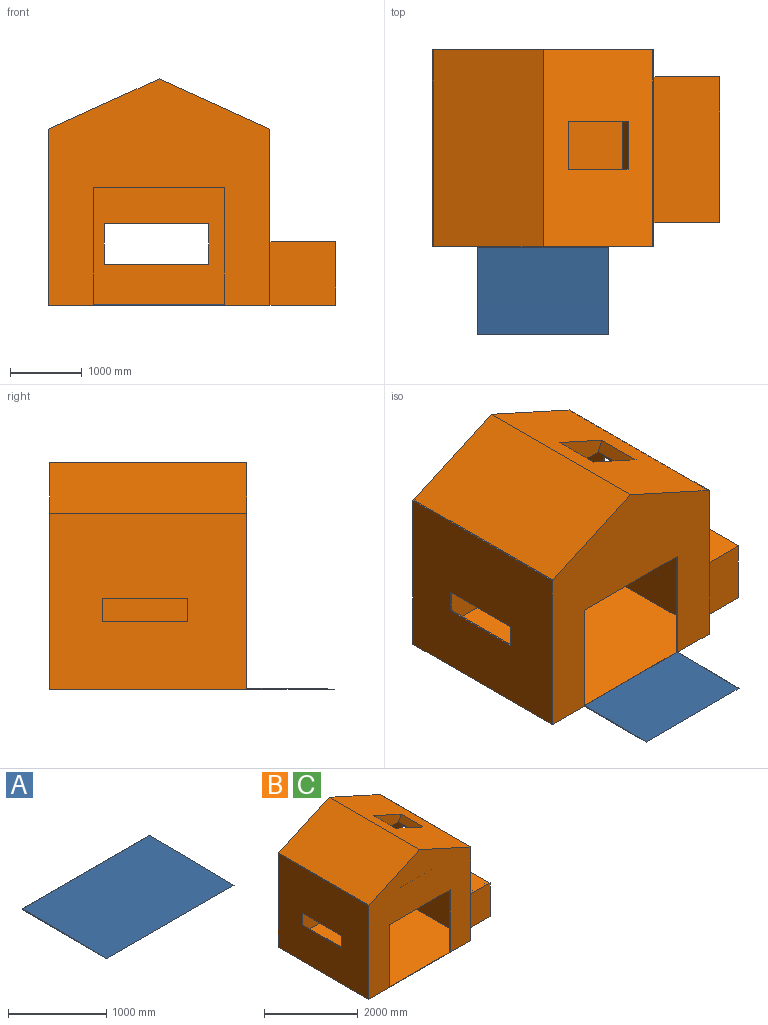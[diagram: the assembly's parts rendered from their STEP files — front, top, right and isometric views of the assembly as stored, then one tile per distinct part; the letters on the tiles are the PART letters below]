
ASSEMBLY  parts=3 mates=1
PART A: 6 faces, bbox 1828.8x1219.2x12.7 mm
  f0: plane 1219.2x12.7mm, normal (-1,0,0), area 10334.8mm2, adj f1,f3,f4,f5
  f1: plane 1828.8x1219.2mm, normal (0,0,-1), area 2229673mm2, adj f0,f2,f4,f5
  f2: plane 1219.2x12.7mm, normal (1,0,0), area 10334.8mm2, adj f1,f3,f4,f5
  f3: plane 1828.8x2.85mm, normal (0,0,1), area 5206.3mm2, adj f0,f2,f4,f5
  f4: plane 1828.8x12.7mm, normal (0,1,0), area 23225.8mm2, adj f0,f1,f2,f3
  f5: cylinder r=58254.97mm len=1828.8mm, axis (-1,0,0), area 2224628.3mm2, adj f0,f1,f2,f3
PART B: 50 faces, bbox 4000.5x2743.2x3149.6 mm
  f0: plane 2743.2x2451.1mm, normal (1,0,0), area 4446398.5mm2, adj f1,f7,f11,f12,f18,f19,f20,f21
  f1: plane 3149.57x3086.1mm, normal (0,1,0), area 7811884.2mm2, adj f0,f3,f7,f10,f11,f29,f30,f31
  f2: plane 3048x2438.4mm, normal (0,-1,0), area 6602012.2mm2, adj f4,f6,f8,f9,f29,f30,f31,f32
  f3: plane 2743.2x2451.1mm, normal (-1,0,0), area 6342757.1mm2, adj f1,f10,f11,f12,f22,f23,f24,f25
  f4: plane 2705.1x2438.4mm, normal (1,0,0), area 6215015.4mm2, adj f2,f8,f9,f13,f22,f23,f24,f25
  f5: plane 1879.6x88.9mm, normal (1,0,0), area 167096.4mm2, adj f11,f42,f43,f44
  f6: plane 2705.1x2438.4mm, normal (-1,0,0), area 6112201.6mm2, adj f2,f8,f9,f13,f18,f19,f20,f21
  f7: plane 2743.2x1543.05mm, normal (0.41,0,0.91), area 4035089.3mm2, adj f0,f1,f10,f12,f14,f15,f16,f17
  f8: plane 3048x2705.1mm, normal (0,0,-1), area 7574170.4mm2, adj f2,f4,f6,f13,f14,f15,f16,f17
  f9: plane 3048x2724.15mm, normal (0,0,1), area 8279983.4mm2, adj f2,f4,f6,f12,f13,f27,f28
  f10: plane 2743.2x1543.05mm, normal (-0.41,0,0.91), area 4646356.3mm2, adj f1,f3,f7,f12
  f11: plane 4000.5x2743.2mm, normal (0,0,-1), area 8605144.1mm2, adj f0,f1,f3,f5,f12,f39,f41,f42
  f12: plane 3149.57x3086.1mm, normal (0,-1,0), area 5669217.8mm2, adj f0,f3,f7,f9,f10,f11,f26,f27
  f13: plane 3048x2438.4mm, normal (0,1,0), area 4459345.9mm2, adj f4,f6,f8,f9,f26,f27,f28
  f14: plane 1073.33x539.15mm, normal (0,-1,0), area 351176.9mm2, adj f7,f8,f15,f17
  f15: plane 671.51x539.15mm, normal (0.91,0,-0.41), area 397408.2mm2, adj f7,f8,f14,f16
  f16: plane 1073.33x539.15mm, normal (0,1,0), area 351176.9mm2, adj f7,f8,f15,f17
  f17: plane 671.51x163.77mm, normal (-0.91,0,0.41), area 120714.5mm2, adj f7,f8,f14,f16
  f18: plane 1195.39x19.05mm, normal (0,0,-1), area 22772.2mm2, adj f0,f6,f19,f21
  f19: plane 404.82x19.05mm, normal (0,1,0), area 7711.8mm2, adj f0,f6,f18,f20
  f20: plane 1195.39x19.05mm, normal (0,0,1), area 22772.2mm2, adj f0,f6,f19,f21
  f21: plane 404.82x19.05mm, normal (0,-1,0), area 7711.8mm2, adj f0,f6,f18,f20
  f22: plane 1188.26x19.05mm, normal (0,0,-1), area 22636.4mm2, adj f3,f4,f23,f25
  f23: plane 320.72x19.05mm, normal (0,-1,0), area 6109.7mm2, adj f3,f4,f22,f24
  f24: plane 1188.26x19.05mm, normal (0,0,1), area 22636.4mm2, adj f3,f4,f23,f25
  f25: plane 320.72x19.05mm, normal (0,1,0), area 6109.7mm2, adj f3,f4,f22,f24
  f26: plane 1828.8x19.05mm, normal (0,0,-1), area 34838.6mm2, adj f12,f13,f27,f28
  f27: plane 1625.6x19.05mm, normal (1,0,0), area 30967.7mm2, adj f9,f12,f13,f26
  f28: plane 1625.6x19.05mm, normal (-1,0,0), area 30967.7mm2, adj f9,f12,f13,f26
  f29: plane 1457.54x19.05mm, normal (0,0,-1), area 27766.1mm2, adj f1,f2,f30,f32
  f30: plane 569.61x19.05mm, normal (-1,0,0), area 10851.1mm2, adj f1,f2,f29,f31
  f31: plane 1457.54x19.05mm, normal (0,0,1), area 27766.1mm2, adj f1,f2,f30,f32
  f32: plane 569.61x19.05mm, normal (1,0,0), area 10851.1mm2, adj f1,f2,f29,f31
  f33: plane 914.4x330.2mm, normal (0,-1,0), area 301934.9mm2, adj f34,f46,f47,f49
  f34: plane 1879.6x914.4mm, normal (0,0,1), area 1718706.2mm2, adj f33,f35,f47,f49
  f35: plane 914.4x330.2mm, normal (0,1,0), area 301934.9mm2, adj f34,f46,f47,f49
  f36: plane 914.4x406.4mm, normal (0,-1,0), area 371612.2mm2, adj f37,f45,f47,f48
  f37: plane 1879.6x914.4mm, normal (0,0,1), area 1718706.2mm2, adj f36,f38,f47,f48
  f38: plane 914.4x406.4mm, normal (0,1,0), area 371612.2mm2, adj f37,f45,f47,f48
  f39: plane 914.4x882.65mm, normal (0,1,0), area 807095.2mm2, adj f0,f11,f40,f47
  f40: plane 2032x914.4mm, normal (0,0,1), area 1858060.8mm2, adj f0,f39,f41,f47
  f41: plane 914.4x882.65mm, normal (0,-1,0), area 807095.2mm2, adj f0,f11,f40,f47
  f42: plane 914.4x88.9mm, normal (0,1,0), area 81290.2mm2, adj f5,f11,f43,f47
  f43: plane 1879.6x914.4mm, normal (0,0,-1), area 1718706.2mm2, adj f5,f42,f44,f47
  f44: plane 914.4x88.9mm, normal (0,-1,0), area 81290.2mm2, adj f5,f11,f43,f47
  f45: plane 1879.6x914.4mm, normal (0,0,-1), area 1718706.2mm2, adj f36,f38,f47,f48
  f46: plane 1879.6x914.4mm, normal (0,0,-1), area 1718706.2mm2, adj f33,f35,f47,f49
  f47: plane 2032x882.65mm, normal (1,0,0), area 241935mm2, adj f11,f33,f34,f35,f36,f37,f38,f39
  f48: plane 1879.6x406.4mm, normal (1,0,0), area 763869.4mm2, adj f36,f37,f38,f45
  f49: plane 1879.6x330.2mm, normal (1,0,0), area 620643.9mm2, adj f33,f34,f35,f46
PART C: same geometry as B
PLACE A t=(-2055.96,-1559.08,-70.66)mm
PLACE B t=(604.6,-187.48,613.35)mm
PLACE C t=(604.6,-187.48,613.35)mm
MATE fastened A.f4 <-> C.f12  axis (0,1,0) through (-2518.28,-1559.08,-58.36)mm
